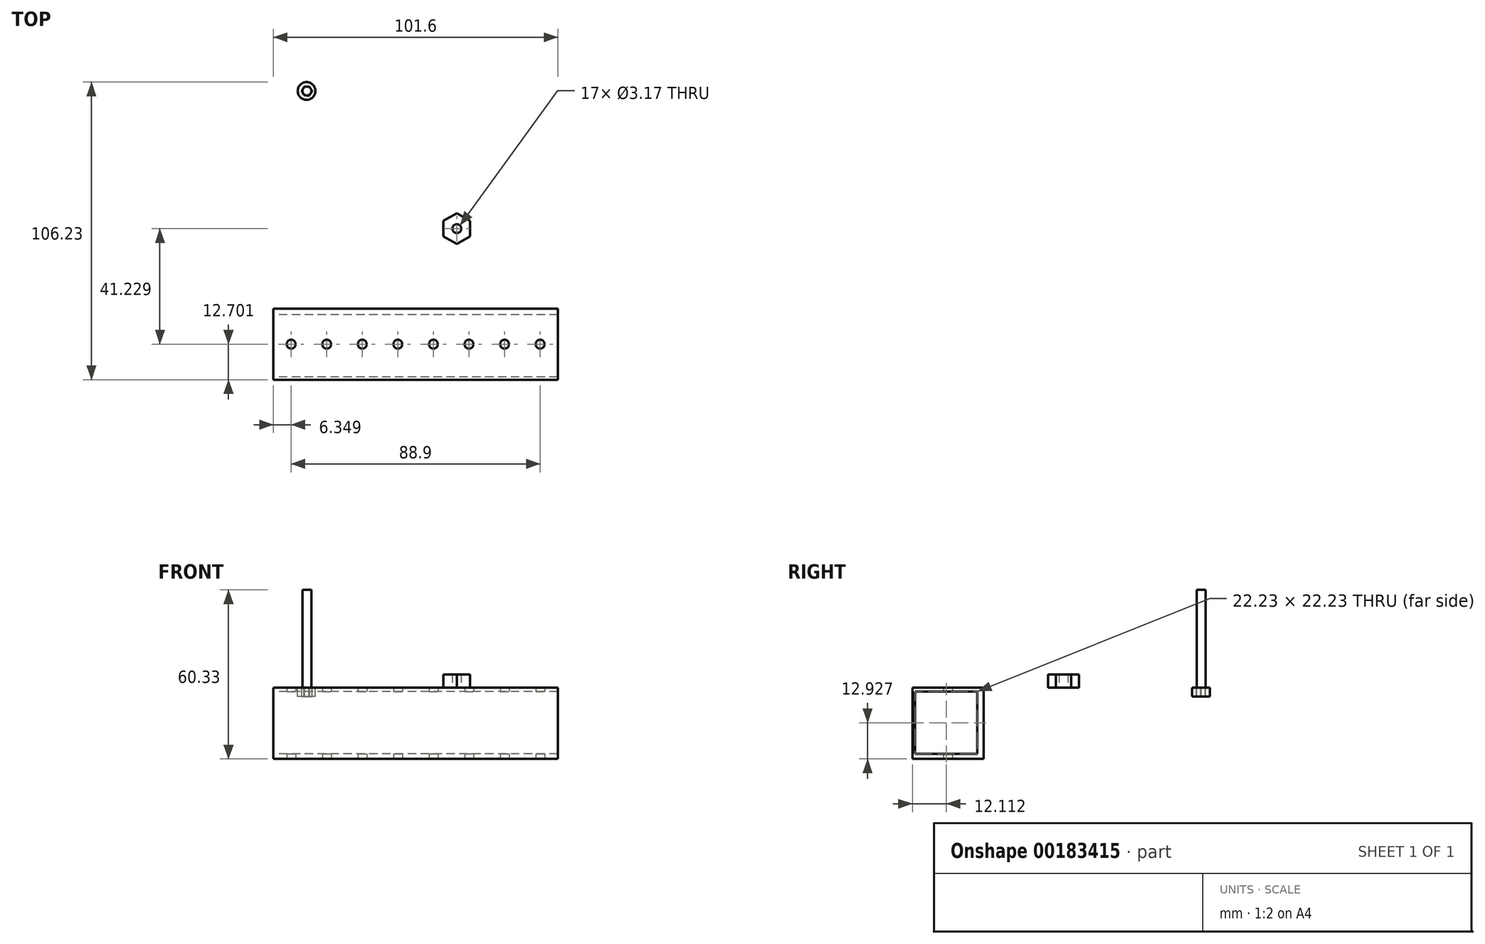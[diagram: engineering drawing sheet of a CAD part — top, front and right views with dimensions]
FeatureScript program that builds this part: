
annotation { "Feature Type Name" : "Feature", "Feature Type Description" : "" }
export const myFeature = defineFeature(function(context is Context, id is Id, definition is map)
    precondition{}
    {
        {
            var Q0;
            Q0=qCreatedBy(makeId("Top.planeOp"),FACE);
            var sketch = newSketch(context, id + "F0", { "sketchPlane" : qUnion([Q0])});
            skCircle(sketch, "E0.cCircle", {"center": v(0, 0) * mm, "radius": 4.76 * mm, "construction": true});
            skLineSegment(sketch, "E0.0", {"start": v(-4.76, -2.75) * mm, "end": v(-4.76, 2.75) * mm});
            skLineSegment(sketch, "E0.1", {"start": v(-4.76, 2.75) * mm, "end": v(0, 5.5) * mm});
            skLineSegment(sketch, "E0.2", {"start": v(0, 5.5) * mm, "end": v(4.76, 2.75) * mm});
            skLineSegment(sketch, "E0.3", {"start": v(4.76, 2.75) * mm, "end": v(4.76, -2.75) * mm});
            skLineSegment(sketch, "E0.4", {"start": v(4.76, -2.75) * mm, "end": v(0, -5.5) * mm});
            skLineSegment(sketch, "E0.5", {"start": v(0, -5.5) * mm, "end": v(-4.76, -2.75) * mm});
            skPoint(sketch, "E0.0.midPoint", {"position": v(-4.76, 0) * mm});
            skCircle(sketch, "E1", {"center": v(0, 0) * mm, "radius": 1.59 * mm});
            skSolve(sketch);
        }
        {
            var Q0;
            Q0=makeQuery(id+"F0.imprint","IMPRINT",FACE,{"disambiguationData":[TD([[makeQuery(id+"F0.imprint","IMPRINT",EDGE,{"derivedFrom":sQuery(id+"F0.wireOp",EDGE,"E0.0")}),-1.0]])]});
            extrude(context, id + "F1", {"entities" : qUnion([Q0]), "depth" : 4.76 * mm});
        }
        {
            var Q0;
            Q0=qCreatedBy(makeId("Top.planeOp"),FACE);
            var sketch = newSketch(context, id + "F2", { "sketchPlane" : qUnion([Q0])});
            skCircle(sketch, "E2", {"center": v(-53.54, 49.14) * mm, "radius": 1.59 * mm});
            skSolve(sketch);
        }
        {
            var Q0;
            Q0=makeQuery(id+"F2.imprint","IMPRINT",FACE,{"disambiguationData":[TD([[makeQuery(id+"F2.imprint","IMPRINT",EDGE,{"derivedFrom":sQuery(id+"F2.wireOp",EDGE,"E2")}),1.0]])]});
            extrude(context, id + "F3", {"entities" : qUnion([Q0]), "depth" : 34.92 * mm});
        }
        {
            var Q0;
            Q0=qCreatedBy(makeId("Top.planeOp"),FACE);
            var sketch = newSketch(context, id + "F4", { "sketchPlane" : qUnion([Q0])});
            skCircle(sketch, "E3", {"center": v(-53.65, 49.12) * mm, "radius": 3.17 * mm});
            skSolve(sketch);
        }
        {
            var Q0;
            Q0=makeQuery(id+"F4.imprint","IMPRINT",FACE,{"disambiguationData":[TD([[makeQuery(id+"F4.imprint","IMPRINT",EDGE,{"derivedFrom":sQuery(id+"F4.wireOp",EDGE,"E3")}),1.0]])]});
            extrude(context, id + "F5", {"entities" : qUnion([Q0]), "operationType" : NewBodyOperationType.ADD, "oppositeDirection" : true, "depth" : 3.17 * mm});
        }
        {
            var Q0;
            Q0=qCreatedBy(makeId("Top.planeOp"),FACE);
            var sketch = newSketch(context, id + "F6", { "sketchPlane" : qUnion([Q0])});
            skCircle(sketch, "E4.cCircle", {"center": v(-53.57, 49.1) * mm, "radius": 1.59 * mm, "construction": true});
            skLineSegment(sketch, "E4.0", {"start": v(-55.4, 49.25) * mm, "end": v(-54.36, 50.76) * mm});
            skLineSegment(sketch, "E4.1", {"start": v(-54.36, 50.76) * mm, "end": v(-52.53, 50.62) * mm});
            skLineSegment(sketch, "E4.2", {"start": v(-52.53, 50.62) * mm, "end": v(-51.74, 48.97) * mm});
            skLineSegment(sketch, "E4.3", {"start": v(-51.74, 48.97) * mm, "end": v(-52.78, 47.45) * mm});
            skLineSegment(sketch, "E4.4", {"start": v(-52.78, 47.45) * mm, "end": v(-54.6, 47.6) * mm});
            skLineSegment(sketch, "E4.5", {"start": v(-54.6, 47.6) * mm, "end": v(-55.4, 49.25) * mm});
            skPoint(sketch, "E4.0.midPoint", {"position": v(-54.88, 50) * mm});
            skSolve(sketch);
        }
        {
            var Q0;
            Q0 = qSketchRegion(id + "F6", true);
            extrude(context, id + "F7", {"entities" : qUnion([Q0]), "operationType" : NewBodyOperationType.REMOVE, "oppositeDirection" : true, "depth" : 3.17 * mm});
        }
        {
            var Q0;
            Q0=qCreatedBy(makeId("Top.planeOp"),FACE);
            var sketch = newSketch(context, id + "F8", { "sketchPlane" : qUnion([Q0])});
            skLineSegment(sketch, "E5.bottom", {"start": v(-65.51, -28.53) * mm, "end": v(36.09, -28.53) * mm});
            skLineSegment(sketch, "E5.top", {"start": v(-65.51, -53.93) * mm, "end": v(36.09, -53.93) * mm});
            skLineSegment(sketch, "E5.left", {"start": v(-65.51, -28.53) * mm, "end": v(-65.51, -53.93) * mm});
            skLineSegment(sketch, "E5.right", {"start": v(36.09, -28.53) * mm, "end": v(36.09, -53.93) * mm});
            skSolve(sketch);
        }
        {
            var Q0;
            Q0 = qSketchRegion(id + "F8", true);
            extrude(context, id + "F9", {"entities" : qUnion([Q0]), "oppositeDirection" : true, "depth" : 25.4 * mm});
        }
        {
            var Q0;
            Q0=makeQuery(id+"F9.opExtrude","SWEPT_FACE",FACE,{"disambiguationData":[OSD([sQuery(id+"F8.wireOp",EDGE,"E5.left")])]});
            var sketch = newSketch(context, id + "F10", { "sketchPlane" : qUnion([Q0])});
            skLineSegment(sketch, "E6.bottom", {"start": v(30.7, -1.36) * mm, "end": v(52.93, -1.36) * mm});
            skLineSegment(sketch, "E6.top", {"start": v(30.7, -23.59) * mm, "end": v(52.93, -23.59) * mm});
            skLineSegment(sketch, "E6.left", {"start": v(30.7, -1.36) * mm, "end": v(30.7, -23.59) * mm});
            skLineSegment(sketch, "E6.right", {"start": v(52.93, -1.36) * mm, "end": v(52.93, -23.59) * mm});
            skSolve(sketch);
        }
        {
            var Q0;
            Q0 = qSketchRegion(id + "F10", true);
            extrude(context, id + "F11", {"entities" : qUnion([Q0]), "operationType" : NewBodyOperationType.REMOVE, "oppositeDirection" : true, "depth" : 101.6 * mm});
        }
        {
            var Q0;
            Q0=makeQuery(id+"F9.opExtrude","CAP_FACE",FACE,{"disambiguationData":[OSD([sQuery(id+"F8.wireOp",EDGE,"E5.bottom"),sQuery(id+"F8.wireOp",EDGE,"E5.top"),sQuery(id+"F8.wireOp",EDGE,"E5.left"),sQuery(id+"F8.wireOp",EDGE,"E5.right")])],"isStart":false});
            var sketch = newSketch(context, id + "F12", { "sketchPlane" : qUnion([Q0])});
            skCircle(sketch, "E7", {"center": v(-59.16, 41.23) * mm, "radius": 1.59 * mm});
            skCircle(sketch, "E8", {"center": v(-46.46, 41.23) * mm, "radius": 1.59 * mm});
            skCircle(sketch, "E9", {"center": v(-33.76, 41.23) * mm, "radius": 1.59 * mm});
            skCircle(sketch, "E10", {"center": v(-21.06, 41.23) * mm, "radius": 1.59 * mm});
            skCircle(sketch, "E11", {"center": v(-8.36, 41.23) * mm, "radius": 1.59 * mm});
            skCircle(sketch, "E12", {"center": v(4.34, 41.23) * mm, "radius": 1.59 * mm});
            skCircle(sketch, "E13", {"center": v(17.04, 41.23) * mm, "radius": 1.59 * mm});
            skCircle(sketch, "E14", {"center": v(29.74, 41.23) * mm, "radius": 1.59 * mm});
            skSolve(sketch);
        }
        {
            var Q0;
            Q0 = qSketchRegion(id + "F12", true);
            extrude(context, id + "F13", {"entities" : qUnion([Q0]), "operationType" : NewBodyOperationType.REMOVE, "oppositeDirection" : true, "depth" : 25.4 * mm});
        }
    });
